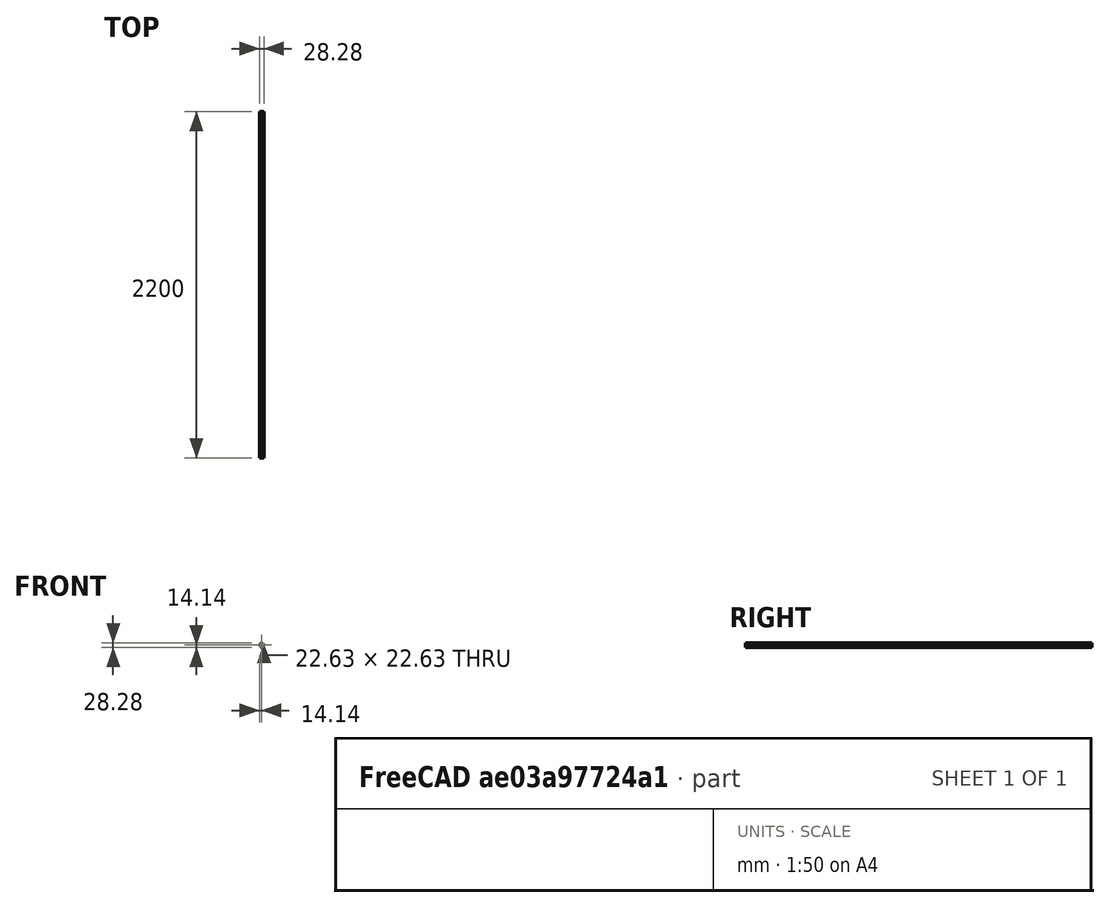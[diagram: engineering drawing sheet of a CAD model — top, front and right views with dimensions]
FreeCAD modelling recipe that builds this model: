
FCSTD DOCUMENT  (FreeCAD 0.15R4671 (Git))
Label: Poutre_centrale_20x20x2_L2200_old
License: All rights reserved
LicenseURL: http://en.wikipedia.org/wiki/All_rights_reserved
objects: Sketcher::SketchObject×1, PartDesign::Pad×1
note: 3 computed .brp shape members not serialized (recipe doc carries the construction recipe); baked Part::Feature solids carry a one-line shape summary decoded from their .brp

FEATURE [Sketcher::SketchObject] Sketch
  Placement = pos=(0,0,0) rot=(1,0,0;1.5708rad)
  sketch-geometry (10):
    g0: LineSegment StartX=14.1421 StartY=0 StartZ=0 EndX=0 EndY=14.1421 EndZ=0
    g1: LineSegment StartX=0 StartY=14.1421 StartZ=0 EndX=-14.1421 EndY=0 EndZ=0
    g2: LineSegment StartX=-14.1421 StartY=0 StartZ=0 EndX=0 EndY=-14.1421 EndZ=0
    g3: LineSegment StartX=0 StartY=-14.1421 StartZ=0 EndX=14.1421 EndY=0 EndZ=0
    g4: Circle [constr] CenterX=0 CenterY=0 CenterZ=0 NormalX=0 NormalY=0 NormalZ=1 Radius=14.1421
    g5: LineSegment StartX=11.3137 StartY=0 StartZ=0 EndX=0 EndY=11.3137 EndZ=0
    g6: LineSegment StartX=0 StartY=11.3137 StartZ=0 EndX=-11.3137 EndY=0 EndZ=0
    g7: LineSegment StartX=-11.3137 StartY=0 StartZ=0 EndX=0 EndY=-11.3137 EndZ=0
    g8: LineSegment StartX=0 StartY=-11.3137 StartZ=0 EndX=11.3137 EndY=0 EndZ=0
    g9: Circle [constr] CenterX=0 CenterY=0 CenterZ=0 NormalX=0 NormalY=0 NormalZ=1 Radius=11.3137
  constraints (30):
    c: Coincident(g0,g1)
    c: Coincident(g1,g2)
    c: Coincident(g2,g3)
    c: Coincident(g3,g0)
    c: Equal(g0,g1)
    c: Equal(g0,g2)
    c: Equal(g0,g3)
    c: PointOnObject(g0,g4)
    c: PointOnObject(g1,g4)
    c: PointOnObject(g2,g4)
    c: PointOnObject(g3,g4)
    c: Coincident(g1,g-1)
    c: Coincident(g5,g6)
    c: Coincident(g6,g7)
    c: Coincident(g7,g8)
    c: Coincident(g8,g5)
    c: Equal(g5,g6)
    c: Equal(g5,g7)
    c: Equal(g5,g8)
    c: PointOnObject(g5,g9)
    c: PointOnObject(g6,g9)
    c: PointOnObject(g7,g9)
    c: PointOnObject(g8,g9)
    c: Coincident(g6,g-1)
    c: Distance(g0,g1) = 20
    c: Coincident(g4,g-1)
    c: Coincident(g9,g-1)
    c: PointOnObject(g0,g-1)
    c: PointOnObject(g5,g-1)
    c: Distance(g5,g5) = 16
FEATURE [PartDesign::Pad] Pad
  Length = 2200
  Length2 = 100
  Midplane = true
  Placement = pos=(0,0,0) rot=(1,0,0;1.5708rad)
  Sketch = -> Sketch
  Type = 0
